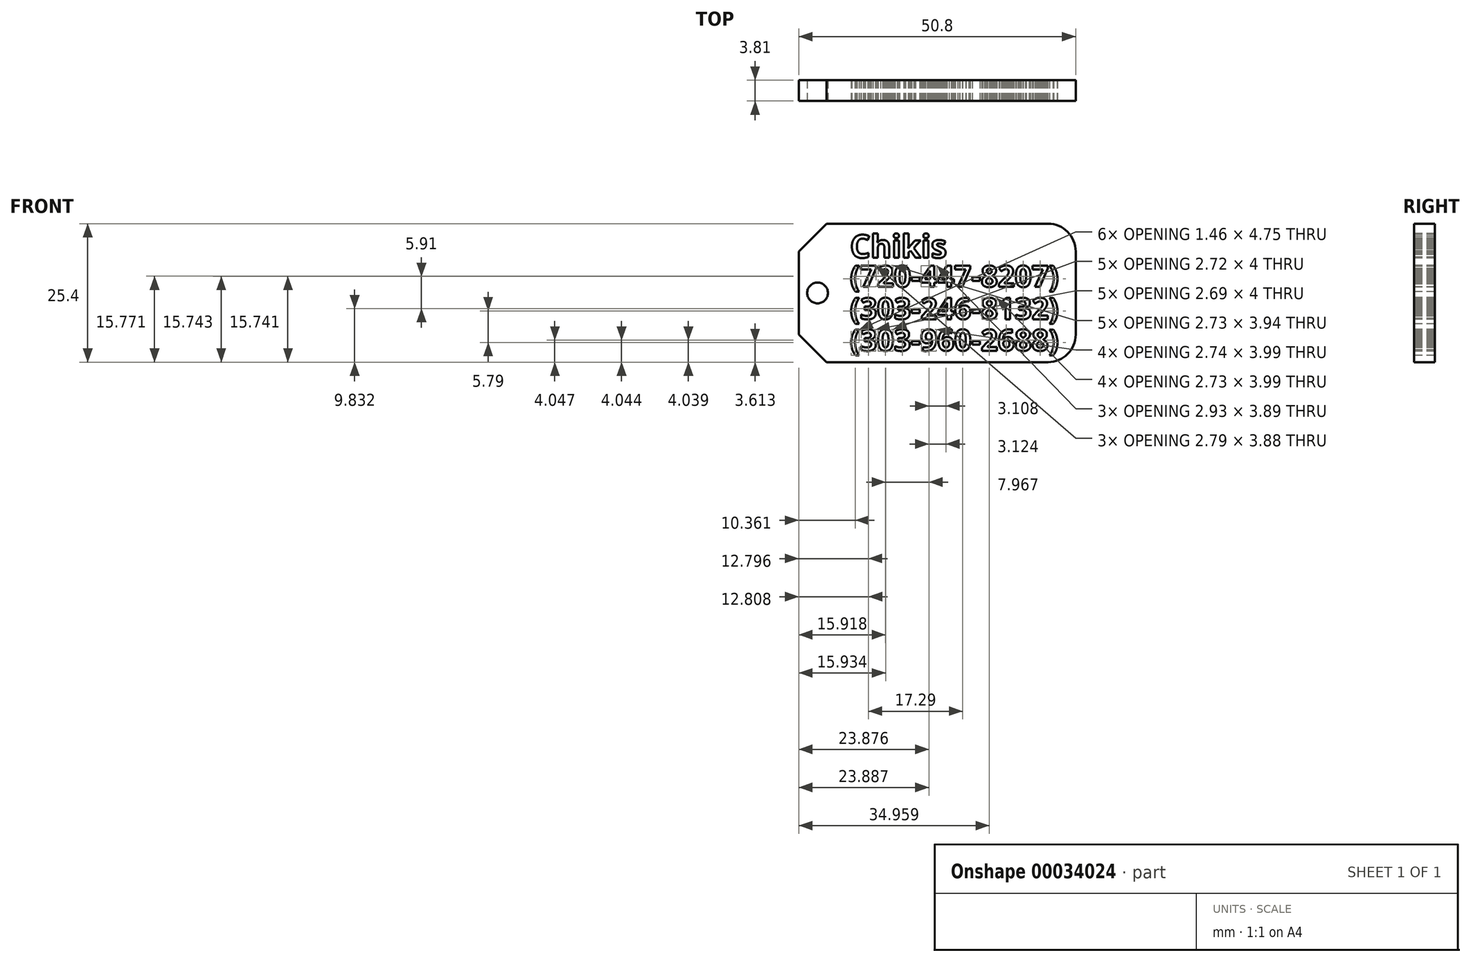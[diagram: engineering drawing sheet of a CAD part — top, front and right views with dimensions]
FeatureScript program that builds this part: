
annotation { "Feature Type Name" : "Feature", "Feature Type Description" : "" }
export const myFeature = defineFeature(function(context is Context, id is Id, definition is map)
    precondition{}
    {
        {
            var Q0;
            Q0=qCreatedBy(makeId("Front.planeOp"),FACE);
            var sketch = newSketch(context, id + "F0", { "sketchPlane" : qUnion([Q0])});
            skLineSegment(sketch, "E0.bottom", {"start": v(-28.11, -0.65) * mm, "end": v(22.69, -0.65) * mm});
            skLineSegment(sketch, "E0.top", {"start": v(-28.11, -26.05) * mm, "end": v(22.69, -26.05) * mm});
            skLineSegment(sketch, "E0.left", {"start": v(-28.11, -0.65) * mm, "end": v(-28.11, -26.05) * mm});
            skLineSegment(sketch, "E0.right", {"start": v(22.69, -0.65) * mm, "end": v(22.69, -26.05) * mm});
            skSolve(sketch);
        }
        {
            var Q0;
            Q0=makeQuery(id+"F0.imprint","IMPRINT",FACE,{"disambiguationData":[TD([[makeQuery(id+"F0.imprint","IMPRINT",EDGE,{"derivedFrom":sQuery(id+"F0.wireOp",EDGE,"E0.bottom")}),-1.0]])]});
            extrude(context, id + "F1", {"entities" : qUnion([Q0]), "depth" : 3.8 * mm});
        }
        {
            var Q0;
            Q0=makeQuery(id+"F1.opExtrude","SWEPT_EDGE",EDGE,{"disambiguationData":[OSD([sQuery(id+"F0.wireOp",EDGE,"E0.bottom"),sQuery(id+"F0.wireOp",EDGE,"E0.left")])]});
            var Q1;
            Q1=makeQuery(id+"F1.opExtrude","SWEPT_EDGE",EDGE,{"disambiguationData":[OSD([sQuery(id+"F0.wireOp",EDGE,"E0.top"),sQuery(id+"F0.wireOp",EDGE,"E0.left")])]});
            chamfer(context, id + "F2", {"entities" : qUnion([Q0, Q1]), "width" : 5.08 * mm, "tangentPropagation" : true});
        }
        {
            var Q0;
            Q0=makeQuery(id+"F1.opExtrude","SWEPT_EDGE",EDGE,{"disambiguationData":[OSD([sQuery(id+"F0.wireOp",EDGE,"E0.bottom"),sQuery(id+"F0.wireOp",EDGE,"E0.right")])]});
            var Q1;
            Q1=makeQuery(id+"F1.opExtrude","SWEPT_EDGE",EDGE,{"disambiguationData":[OSD([sQuery(id+"F0.wireOp",EDGE,"E0.top"),sQuery(id+"F0.wireOp",EDGE,"E0.right")])]});
            fillet(context, id + "F3", {"entities" : qUnion([Q0, Q1]), "radius" : 5.08 * mm, "tangentPropagation" : true, "allowEdgeOverflow" : false});
        }
        {
            var Q0;
            Q0=makeQuery(id+"F1.opExtrude","CAP_FACE",FACE,{"disambiguationData":[OSD([sQuery(id+"F0.wireOp",EDGE,"E0.bottom"),sQuery(id+"F0.wireOp",EDGE,"E0.top"),sQuery(id+"F0.wireOp",EDGE,"E0.left"),sQuery(id+"F0.wireOp",EDGE,"E0.right")])],"isStart":false});
            var sketch = newSketch(context, id + "F4", { "sketchPlane" : qUnion([Q0])});
            skSolve(sketch);
        }
        {
            var Q0;
            {var subQ3=sQuery(id+"F0.wireOp",EDGE,"E0.left");Q0=makeQuery(id+"F4.imprint","IMPRINT",FACE,{"disambiguationData":[TD([[makeQuery(id+"F4.imprint","IMPRINT",EDGE,{"derivedFrom":makeQuery(id+"F1.opExtrude","CAP_EDGE",EDGE,{"disambiguationData":[OSD([subQ3])],"isStart":false})}),1.0]])]});}
            var sketch = newSketch(context, id + "F5", { "sketchPlane" : qUnion([Q0])});
            skCircle(sketch, "E1", {"center": v(-24.66, -13.35) * mm, "radius": 1.9 * mm});
            skSolve(sketch);
        }
        {
            var Q0;
            Q0 = qSketchRegion(id + "F5", true);
            extrude(context, id + "F6", {"entities" : qUnion([Q0]), "operationType" : NewBodyOperationType.REMOVE, "oppositeDirection" : true, "depth" : 25.4 * mm});
        }
        {
            var Q0;
            {var subQ3=sQuery(id+"F0.wireOp",EDGE,"E0.left");Q0=makeQuery(id+"F4.imprint","IMPRINT",FACE,{"disambiguationData":[TD([[makeQuery(id+"F4.imprint","IMPRINT",EDGE,{"derivedFrom":makeQuery(id+"F1.opExtrude","CAP_EDGE",EDGE,{"disambiguationData":[OSD([subQ3])],"isStart":false})}),1.0]])]});}
            var sketch = newSketch(context, id + "F7", { "sketchPlane" : qUnion([Q0])});
            skText(sketch, "E2", { "text": "Chikis", "fontName": "OpenSans-Bold.ttf"});
            skText(sketch, "E3", { "text": "(720-447-8207)", "fontName": "OpenSans-Bold.ttf"});
            skText(sketch, "E4", { "text": "(303-246-8132)", "fontName": "OpenSans-Bold.ttf"});
            skText(sketch, "E5", { "text": "(303-960-2688)", "fontName": "OpenSans-Bold.ttf"});
            const initialGuessF7  = {"E2": [-0.0187, -0.0069, 1, 0, 0.00423], "E3": [-0.0187, -0.01225, 1, 0, 0.00392], "E4": [-0.0187, -0.01816, 1, 0, 0.00392], "E5": [-0.0187, -0.02395, 1, 0, 0.00392]};
            skSetInitialGuess(sketch, initialGuessF7);
            skSolve(sketch);
        }
        {
            var Q0;
            Q0 = qSketchRegion(id + "F7", true);
            extrude(context, id + "F8", {"entities" : qUnion([Q0]), "operationType" : NewBodyOperationType.REMOVE, "endBound" : BoundingType.THROUGH_ALL, "oppositeDirection" : true, "depth" : 25.4 * mm});
        }
    });
